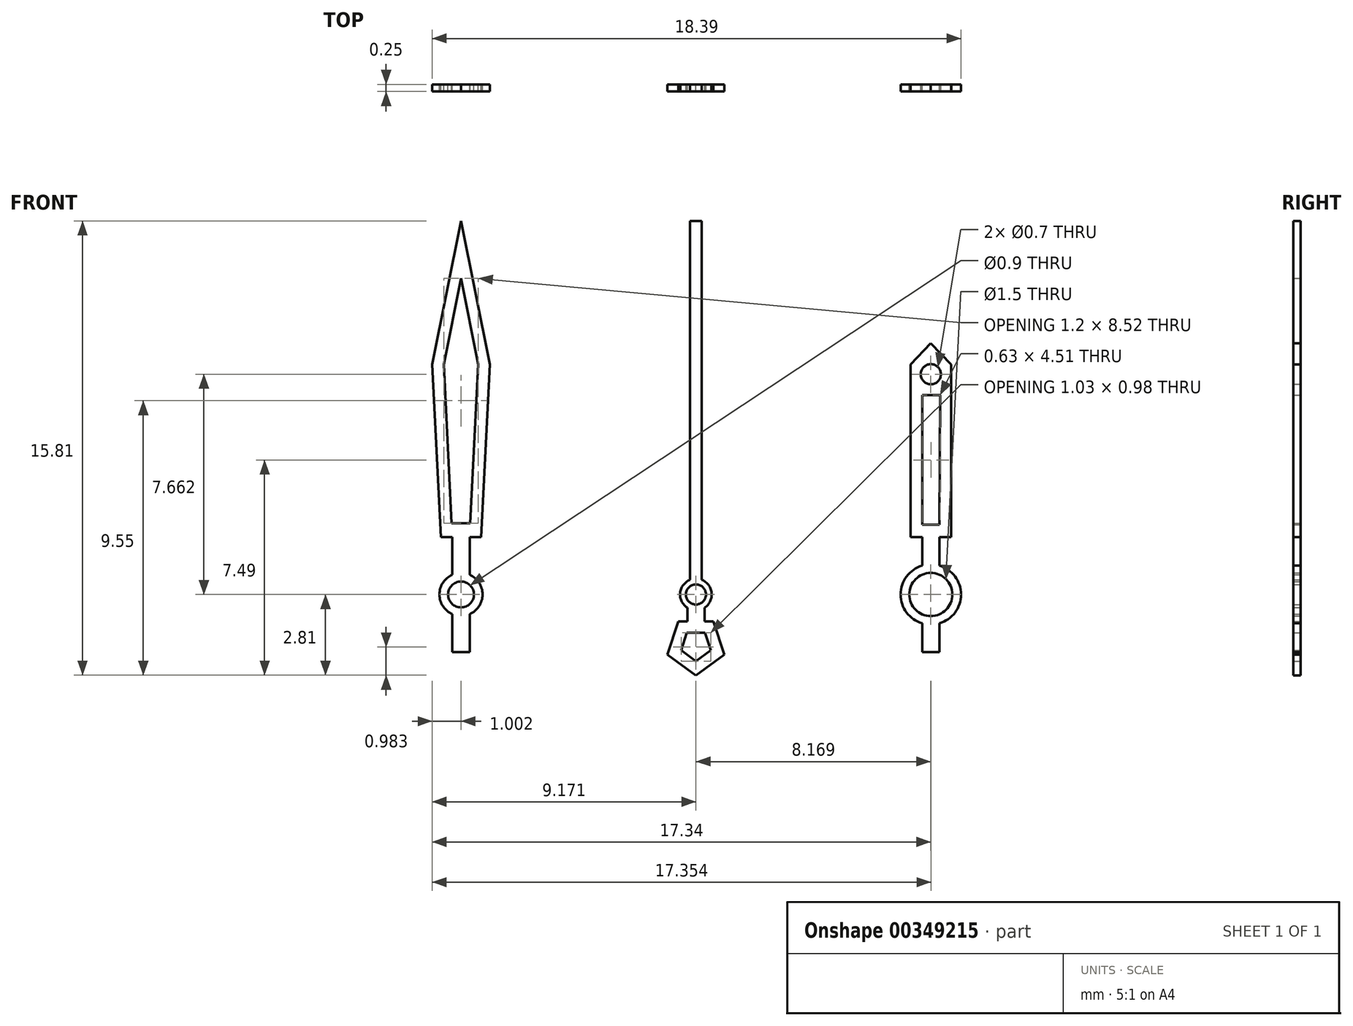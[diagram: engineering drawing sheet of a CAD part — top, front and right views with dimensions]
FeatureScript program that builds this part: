
annotation { "Feature Type Name" : "Feature", "Feature Type Description" : "" }
export const myFeature = defineFeature(function(context is Context, id is Id, definition is map)
    precondition{}
    {
        {
            var Q0;
            Q0=qCreatedBy(makeId("Front.planeOp"),FACE);
            var sketch = newSketch(context, id + "F0", { "sketchPlane" : qUnion([Q0])});
            skLineSegment(sketch, "E0", {"start": v(-36.59, 13) * mm, "end": v(-35.59, 8) * mm});
            skCircle(sketch, "E1", {"center": v(-36.59, 0) * mm, "radius": 0.45 * mm});
            skCircle(sketch, "E2.0", {"center": v(-36.59, 0) * mm, "radius": 0.75 * mm});
            skLineSegment(sketch, "E3.MirrorCS", {"start": v(-36.59, 13) * mm, "end": v(-37.59, 8) * mm});
            skLineSegment(sketch, "E4", {"start": v(-36.29, 0.69) * mm, "end": v(-36.29, 2) * mm});
            skLineSegment(sketch, "E5", {"start": v(-36.29, -0.69) * mm, "end": v(-36.29, -2) * mm});
            skLineSegment(sketch, "E6.MirrorCS", {"start": v(-36.89, 0.69) * mm, "end": v(-36.89, 2) * mm});
            skLineSegment(sketch, "E7.MirrorCS", {"start": v(-36.89, -0.69) * mm, "end": v(-36.89, -2) * mm});
            skLineSegment(sketch, "E8", {"start": v(-36.89, -2) * mm, "end": v(-36.29, -2) * mm});
            skCircle(sketch, "E9", {"center": v(-20.25, 0) * mm, "radius": 0.75 * mm});
            skCircle(sketch, "E10", {"center": v(-20.25, 0) * mm, "radius": 1.05 * mm});
            skLineSegment(sketch, "E11", {"start": v(-20.25, 8.74) * mm, "end": v(-19.55, 8) * mm});
            skLineSegment(sketch, "E12", {"start": v(-19.55, 8) * mm, "end": v(-19.55, 2) * mm});
            skLineSegment(sketch, "E13", {"start": v(-19.95, 1) * mm, "end": v(-19.95, 2) * mm});
            skLineSegment(sketch, "E14.MirrorCS", {"start": v(-20.95, 8) * mm, "end": v(-20.95, 2) * mm});
            skLineSegment(sketch, "E15.MirrorCS", {"start": v(-20.55, 1) * mm, "end": v(-20.55, 2) * mm});
            skLineSegment(sketch, "E16", {"start": v(-20.95, 2) * mm, "end": v(-20.55, 2) * mm});
            skLineSegment(sketch, "E17", {"start": v(-19.95, 2) * mm, "end": v(-19.55, 2) * mm});
            skLineSegment(sketch, "E18", {"start": v(-20.55, -2) * mm, "end": v(-19.95, -2) * mm});
            skLineSegment(sketch, "E19", {"start": v(-20.55, -1) * mm, "end": v(-20.55, -2) * mm});
            skLineSegment(sketch, "E20", {"start": v(-19.95, -1) * mm, "end": v(-19.95, -2) * mm});
            skLineSegment(sketch, "E21", {"start": v(-36.29, 2) * mm, "end": v(-35.89, 2) * mm});
            skLineSegment(sketch, "E22", {"start": v(-35.59, 8) * mm, "end": v(-35.89, 2) * mm});
            skLineSegment(sketch, "E23.MirrorCS", {"start": v(-37.59, 8) * mm, "end": v(-37.29, 2) * mm});
            skLineSegment(sketch, "E24", {"start": v(-36.89, 2) * mm, "end": v(-37.29, 2) * mm});
            skCircle(sketch, "E25", {"center": v(-28.42, 0) * mm, "radius": 0.35 * mm});
            skCircle(sketch, "E26", {"center": v(-28.42, 0) * mm, "radius": 0.55 * mm});
            skLineSegment(sketch, "E27.0", {"start": v(-28.22, 0) * mm, "end": v(-28.22, 13) * mm});
            skLineSegment(sketch, "E28.MirrorCS", {"start": v(-28.62, 0) * mm, "end": v(-28.62, 13) * mm});
            skLineSegment(sketch, "E29.MirrorCS", {"start": v(-28.72, 0) * mm, "end": v(-28.72, -1.78) * mm});
            skLineSegment(sketch, "E30", {"start": v(-28.62, 13) * mm, "end": v(-28.22, 13) * mm});
            skLineSegment(sketch, "E31", {"start": v(-36.89, 2) * mm, "end": v(-36.29, 2) * mm});
            skLineSegment(sketch, "E32", {"start": v(-36.89, 2) * mm, "end": v(-37.19, 8) * mm});
            skLineSegment(sketch, "E33", {"start": v(-37.19, 8) * mm, "end": v(-36.59, 11) * mm});
            skLineSegment(sketch, "E34", {"start": v(-36.59, 11) * mm, "end": v(-35.99, 8) * mm});
            skLineSegment(sketch, "E35", {"start": v(-35.99, 8) * mm, "end": v(-36.29, 2) * mm});
            skLineSegment(sketch, "E36", {"start": v(-36.91, 2.48) * mm, "end": v(-36.26, 2.48) * mm});
            skLineSegment(sketch, "E37", {"start": v(-20.55, 2) * mm, "end": v(-20.55, 6.94) * mm});
            skLineSegment(sketch, "E38", {"start": v(-19.92, 6.94) * mm, "end": v(-19.95, 2) * mm});
            skLineSegment(sketch, "E39", {"start": v(-20.55, 2.43) * mm, "end": v(-19.95, 2.42) * mm});
            skLineSegment(sketch, "E40", {"start": v(-20.55, 6.94) * mm, "end": v(-19.92, 6.94) * mm});
            skLineSegment(sketch, "E41", {"start": v(-20.95, 8) * mm, "end": v(-20.25, 8.74) * mm});
            skLineSegment(sketch, "E42", {"start": v(-20.25, 8.74) * mm, "end": v(-20.25, 6.94) * mm});
            skCircle(sketch, "E43", {"center": v(-20.25, 7.66) * mm, "radius": 0.35 * mm});
            skLineSegment(sketch, "E44", {"start": v(-28.42, 0) * mm, "end": v(-28.42, -4.67) * mm});
            skLineSegment(sketch, "E45", {"start": v(-28.12, -1.78) * mm, "end": v(-28.12, 0) * mm});
            skCircle(sketch, "E46.cCircle", {"center": v(-28.42, -1.78) * mm, "radius": 0.84 * mm, "construction": true});
            skLineSegment(sketch, "E46.0", {"start": v(-29.03, -0.94) * mm, "end": v(-27.8, -0.94) * mm});
            skLineSegment(sketch, "E46.1", {"start": v(-27.8, -0.94) * mm, "end": v(-27.43, -2.1) * mm});
            skLineSegment(sketch, "E46.2", {"start": v(-27.43, -2.1) * mm, "end": v(-28.42, -2.81) * mm});
            skLineSegment(sketch, "E46.3", {"start": v(-28.42, -2.81) * mm, "end": v(-29.4, -2.1) * mm});
            skLineSegment(sketch, "E46.4", {"start": v(-29.4, -2.1) * mm, "end": v(-29.03, -0.94) * mm});
            skPoint(sketch, "E46.0.midPoint", {"position": v(-28.42, -0.94) * mm});
            skPoint(sketch, "E47.0.midPoint", {"position": v(-28.42, -1.24) * mm});
            skCircle(sketch, "E48.cCircle", {"center": v(-28.42, -1.78) * mm, "radius": 0.44 * mm, "construction": true});
            skLineSegment(sketch, "E48.0", {"start": v(-28.74, -1.34) * mm, "end": v(-28.1, -1.34) * mm});
            skLineSegment(sketch, "E48.1", {"start": v(-28.1, -1.34) * mm, "end": v(-27.9, -1.94) * mm});
            skLineSegment(sketch, "E48.2", {"start": v(-27.9, -1.94) * mm, "end": v(-28.42, -2.32) * mm});
            skLineSegment(sketch, "E48.3", {"start": v(-28.42, -2.32) * mm, "end": v(-28.93, -1.94) * mm});
            skLineSegment(sketch, "E48.4", {"start": v(-28.93, -1.94) * mm, "end": v(-28.74, -1.34) * mm});
            skPoint(sketch, "E48.0.midPoint", {"position": v(-28.42, -1.34) * mm});
            skLineSegment(sketch, "E49", {"start": v(-20.25, 0) * mm, "end": v(-36.59, 0) * mm});
            skSolve(sketch);
        }
        {
            var Q0;
            Q0 = qSketchRegion(id + "F0", true);
            var Q1;
            {var subQ0=sQuery(id+"F0.wireOp",EDGE,"d177a6a1-e401-462f-85d2-7b86f48335750.MirrorCS");var subQ1=sQuery(id+"F0.wireOp",EDGE,"E29.MirrorCS");var subQ2=makeQuery(id+"F0.imprint","INTERSECT",VERTEX,{"derivedFrom":[subQ1,subQ0]});Q1=makeQuery(id+"F0.imprint","IMPRINT",FACE,{"disambiguationData":[TD([[makeQuery(id+"F0.imprint","IMPRINT",EDGE,{"disambiguationData":[TD([[subQ2,1.0]])],"derivedFrom":subQ1}),1.0]])]});}
            var Q2;
            {var subQ0=sQuery(id+"F0.wireOp",EDGE,"RracIFim-sfU7-J9re-uFhn-TZIEqMmSXRwO");var subQ1=sQuery(id+"F0.wireOp",EDGE,"E45");var subQ2=makeQuery(id+"F0.imprint","INTERSECT",VERTEX,{"derivedFrom":[subQ1,subQ0]});Q2=makeQuery(id+"F0.imprint","IMPRINT",FACE,{"disambiguationData":[TD([[makeQuery(id+"F0.imprint","IMPRINT",EDGE,{"disambiguationData":[TD([[subQ2,-1.0]])],"derivedFrom":subQ1}),1.0]])]});}
            extrude(context, id + "F1", {"entities" : qUnion([Q0, Q1, Q2]), "depth" : .25 * mm});
        }
    });
